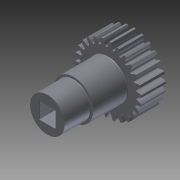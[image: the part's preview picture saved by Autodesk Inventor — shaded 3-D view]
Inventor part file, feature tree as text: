
AUTODESK INVENTOR PART (.ipt)
format: ipt  version: 2013 (Build 170138000, 138)  size: 974,848 bytes
history: native  units: in
note: dims shown in document units (in); Inventor stores cm internally (conversion verified against a paired STEP export)
features: extrude x6, sketch x6, fillet x3
ambient origin geometry x8: Origin, YZ Plane, XZ Plane, XY Plane, X Axis, Y Axis, Z Axis, Center Point
bodies: Solid1 (feature_tree)
feature tree (15):
  extrude  "Extrusion1"  Depth=0.209in TaperAngle=0.0deg
  extrude  "Extrusion2"  Depth=0.276in TaperAngle=0.0deg
  extrude  "Extrusion3"  Depth=0.005in
  fillet  "Fillet1"  Radius=0.005in
  fillet  "Fillet2"  Radius=0.236in
  extrude  "Extrusion4"  Depth=0.059in TaperAngle=0.0deg
  fillet  "Fillet3"  Radius=0.157in
  extrude  "Extrusion5"  [1 undecoded]
  extrude  "Extrusion6"  [1 undecoded]
  sketch  "Sketch1"  dims[d0=0.276in d1=0.209in d2=0.0in]
  sketch  "Sketch2"  dims[d3=0.315in d4=0.276in d5=0.0in]
  sketch  "Sketch3"  dims[d6=0.197in d7=0.0in d8=0.005in d9=0.005in d10=0.236in d11=0.0in]
  sketch  "Sketch4"  dims[d12=0.004in d13=0.059in d14=0.0in d15=0.157in]
  sketch  "Sketch5"  dims[d16=0.276in d17=0.0in]
  sketch  "Sketch6"
note: 2 required parameter values undecoded (feature->parameter linkage not recoverable at this tier; creation-order binding heuristic only, values carry confidence <= 0.55)
